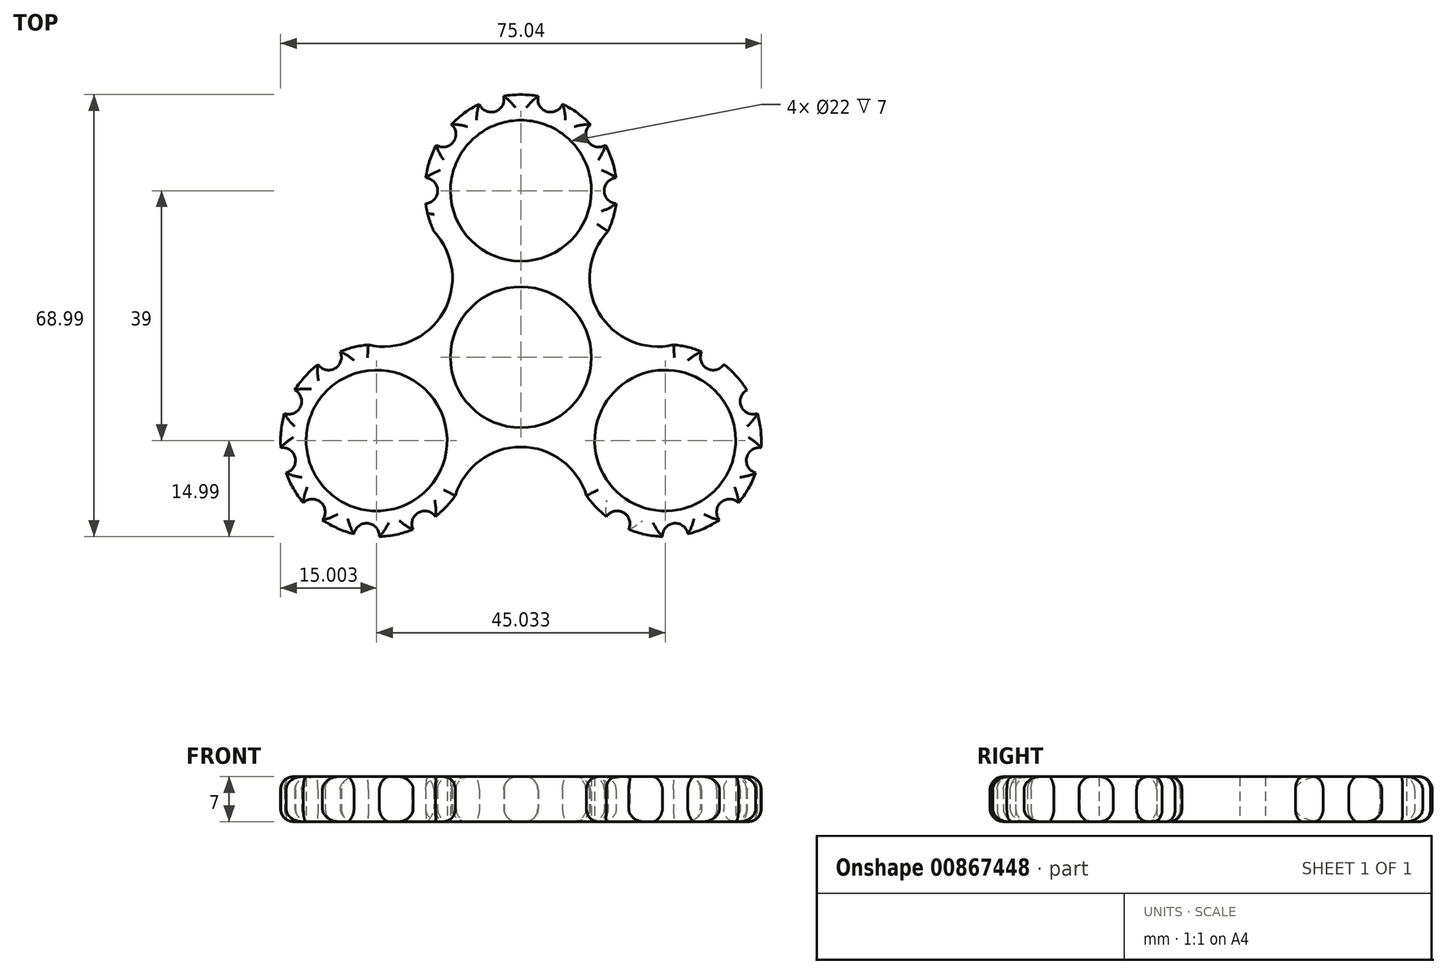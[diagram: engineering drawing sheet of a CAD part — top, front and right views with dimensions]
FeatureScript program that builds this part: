
annotation { "Feature Type Name" : "Feature", "Feature Type Description" : "" }
export const myFeature = defineFeature(function(context is Context, id is Id, definition is map)
    precondition{}
    {
        {
            var Q0;
            Q0=qCreatedBy(makeId("Top.planeOp"),FACE);
            var sketch = newSketch(context, id + "F0", { "sketchPlane" : qUnion([Q0])});
            skCircle(sketch, "E0", {"center": v(0, 0) * mm, "radius": 11 * mm});
            skCircle(sketch, "E1.0", {"center": v(0, 0) * mm, "radius": 14 * mm});
            skLineSegment(sketch, "E2", {"start": v(0, 0) * mm, "end": v(0, 26) * mm});
            skCircle(sketch, "E3", {"center": v(0, 26) * mm, "radius": 11 * mm});
            skCircle(sketch, "E4.0", {"center": v(0, 26) * mm, "radius": 15 * mm});
            skCircle(sketch, "E5", {"center": v(-15, 26) * mm, "radius": 2 * mm});
            skCircle(sketch, "E6.1.0", {"center": v(-12.14, 34.82) * mm, "radius": 2 * mm});
            skCircle(sketch, "E6.2.0", {"center": v(-4.64, 40.27) * mm, "radius": 2 * mm});
            skLineSegment(sketch, "E6.anchor1", {"start": v(0, 26) * mm, "end": v(-15, 26) * mm, "construction": true});
            skLineSegment(sketch, "E6.anchor2", {"start": v(0, 26) * mm, "end": v(15, 26) * mm, "construction": true});
            skCircle(sketch, "E7.1.3.0", {"center": v(4.64, 40.27) * mm, "radius": 2 * mm});
            skCircle(sketch, "E7.1.4.0", {"center": v(12.14, 34.82) * mm, "radius": 2 * mm});
            skPoint(sketch, "E8.center", {"position": v(-0.5, -0.29) * mm});
            skPoint(sketch, "E9", {"position": v(-14.87, 24) * mm});
            skLineSegment(sketch, "E10", {"start": v(0, 0) * mm, "end": v(12.12, 7) * mm});
            skPoint(sketch, "E11.MirrorP", {"position": v(14.87, 24) * mm});
            skCircle(sketch, "E12.1.5.0", {"center": v(15, 26) * mm, "radius": 2 * mm});
            skLineSegment(sketch, "E13", {"start": v(0, 26) * mm, "end": v(13.6, 19.66) * mm});
            skCircle(sketch, "E14.1.0", {"center": v(-22.52, -13) * mm, "radius": 15 * mm});
            skCircle(sketch, "E14.1.1", {"center": v(-22.52, -13) * mm, "radius": 11 * mm});
            skCircle(sketch, "E14.1.2", {"center": v(-15.02, -26) * mm, "radius": 2 * mm});
            skCircle(sketch, "E14.1.3", {"center": v(-24.08, -27.92) * mm, "radius": 2 * mm});
            skCircle(sketch, "E14.1.4", {"center": v(-32.55, -24.15) * mm, "radius": 2 * mm});
            skCircle(sketch, "E14.1.5", {"center": v(-37.19, -16.12) * mm, "radius": 2 * mm});
            skCircle(sketch, "E14.1.6", {"center": v(-36.22, -6.9) * mm, "radius": 2 * mm});
            skCircle(sketch, "E14.1.7", {"center": v(-30.02, 0) * mm, "radius": 2 * mm});
            skCircle(sketch, "E14.2.0", {"center": v(22.52, -13) * mm, "radius": 15 * mm});
            skCircle(sketch, "E14.2.1", {"center": v(22.52, -13) * mm, "radius": 11 * mm});
            skCircle(sketch, "E14.2.2", {"center": v(30.02, 0) * mm, "radius": 2 * mm});
            skCircle(sketch, "E14.2.3", {"center": v(36.22, -6.9) * mm, "radius": 2 * mm});
            skCircle(sketch, "E14.2.4", {"center": v(37.19, -16.12) * mm, "radius": 2 * mm});
            skCircle(sketch, "E14.2.5", {"center": v(32.55, -24.15) * mm, "radius": 2 * mm});
            skCircle(sketch, "E14.2.6", {"center": v(24.08, -27.92) * mm, "radius": 2 * mm});
            skCircle(sketch, "E14.2.7", {"center": v(15.02, -26) * mm, "radius": 2 * mm});
            skLineSegment(sketch, "E15.MirrorCS", {"start": v(22.52, -13) * mm, "end": v(23.82, 1.94) * mm});
            skArc(sketch, "E16", {"start": v(13.6, 19.66) * mm, "mid": v(12.12, 7) * mm, "end": v(23.82, 1.94) * mm});
            skArc(sketch, "E17.1.0", {"start": v(-23.82, 1.94) * mm, "mid": v(-12.12, 7) * mm, "end": v(-13.6, 19.66) * mm});
            skArc(sketch, "E17.2.0", {"start": v(10.23, -21.6) * mm, "mid": v(0, -14) * mm, "end": v(-10.23, -21.6) * mm});
            skSolve(sketch);
        }
        {
            var Q0;
            {var subQ3=sQuery(id+"F0.wireOp",EDGE,"E1.0");var subQ18=sQuery(id+"F0.wireOp",EDGE,"E2");var subQ19=makeQuery(id+"F0.imprint","INTERSECT",VERTEX,{"derivedFrom":[subQ3,subQ18]});Q0=makeQuery(id+"F0.imprint","IMPRINT",FACE,{"disambiguationData":[TD([[makeQuery(id+"F0.imprint","IMPRINT",EDGE,{"disambiguationData":[TD([[subQ19,-1.0]])],"derivedFrom":subQ3}),-1.0]])]});}
            var Q1;
            {var subQ5=sQuery(id+"F0.wireOp",EDGE,"E1.0");var subQ7=sQuery(id+"F0.wireOp",EDGE,"E4.0");var subQ8=makeQuery(id+"F0.imprint","INTERSECT",VERTEX,{"disambiguationData":[OD(0.0)],"derivedFrom":[subQ5,subQ7]});Q1=makeQuery(id+"F0.imprint","IMPRINT",FACE,{"disambiguationData":[TD([[makeQuery(id+"F0.imprint","IMPRINT",EDGE,{"disambiguationData":[TD([[subQ8,-1.0]])],"derivedFrom":subQ5}),-1.0]])]});}
            var Q2;
            {var subQ0=sQuery(id+"F0.wireOp",EDGE,"E4.0");var subQ1=sQuery(id+"F0.wireOp",EDGE,"E1.0");var subQ2=makeQuery(id+"F0.imprint","INTERSECT",VERTEX,{"disambiguationData":[OD(0.0)],"derivedFrom":[subQ1,subQ0]});Q2=makeQuery(id+"F0.imprint","IMPRINT",FACE,{"disambiguationData":[TD([[makeQuery(id+"F0.imprint","IMPRINT",EDGE,{"disambiguationData":[TD([[subQ2,-1.0]])],"derivedFrom":subQ1}),1.0]])]});}
            var Q3;
            {var subQ0=sQuery(id+"F0.wireOp",EDGE,"E2");var subQ1=sQuery(id+"F0.wireOp",EDGE,"E1.0");var subQ2=makeQuery(id+"F0.imprint","INTERSECT",VERTEX,{"derivedFrom":[subQ1,subQ0]});Q3=makeQuery(id+"F0.imprint","IMPRINT",FACE,{"disambiguationData":[TD([[makeQuery(id+"F0.imprint","IMPRINT",EDGE,{"disambiguationData":[TD([[subQ2,-1.0]])],"derivedFrom":subQ1}),1.0]])]});}
            var Q4;
            {var subQ0=sQuery(id+"F0.wireOp",EDGE,"E17.1.0");var subQ1=sQuery(id+"F0.wireOp",EDGE,"E1.0");var subQ2=makeQuery(id+"F0.imprint","INTERSECT",VERTEX,{"derivedFrom":[subQ1,subQ0]});Q4=makeQuery(id+"F0.imprint","IMPRINT",FACE,{"disambiguationData":[TD([[makeQuery(id+"F0.imprint","IMPRINT",EDGE,{"disambiguationData":[TD([[subQ2,1.0]])],"derivedFrom":subQ1}),-1.0]])]});}
            var Q5;
            {var subQ1=sQuery(id+"F0.wireOp",EDGE,"E1.0");var subQ5=makeQuery(id+"F0.imprint","INTERSECT",VERTEX,{"derivedFrom":[subQ1,sQuery(id+"F0.wireOp",EDGE,"E17.1.0")]});Q5=makeQuery(id+"F0.imprint","IMPRINT",FACE,{"disambiguationData":[TD([[makeQuery(id+"F0.imprint","IMPRINT",EDGE,{"disambiguationData":[TD([[subQ5,1.0]])],"derivedFrom":subQ1}),1.0]])]});}
            var Q6;
            {var subQ0=sQuery(id+"F0.wireOp",EDGE,"E17.1.0");var subQ1=sQuery(id+"F0.wireOp",EDGE,"E1.0");var subQ2=makeQuery(id+"F0.imprint","INTERSECT",VERTEX,{"derivedFrom":[subQ1,subQ0]});Q6=makeQuery(id+"F0.imprint","IMPRINT",FACE,{"disambiguationData":[TD([[makeQuery(id+"F0.imprint","IMPRINT",EDGE,{"disambiguationData":[TD([[subQ2,-1.0]])],"derivedFrom":subQ1}),-1.0]])]});}
            var Q7;
            Q7=makeQuery(id+"F0.imprint","IMPRINT",FACE,{"disambiguationData":[TD([[makeQuery(id+"F0.imprint","IMPRINT",EDGE,{"derivedFrom":sQuery(id+"F0.wireOp",EDGE,"E14.1.1")}),-1.0]])]});
            var Q8;
            {var subQ0=sQuery(id+"F0.wireOp",EDGE,"E14.1.0");var subQ1=sQuery(id+"F0.wireOp",EDGE,"E1.0");var subQ2=makeQuery(id+"F0.imprint","INTERSECT",VERTEX,{"disambiguationData":[OD(0.0)],"derivedFrom":[subQ1,subQ0]});Q8=makeQuery(id+"F0.imprint","IMPRINT",FACE,{"disambiguationData":[TD([[makeQuery(id+"F0.imprint","IMPRINT",EDGE,{"disambiguationData":[TD([[subQ2,-1.0]])],"derivedFrom":subQ1}),1.0]])]});}
            var Q9;
            {var subQ0=sQuery(id+"F0.wireOp",EDGE,"E14.1.0");var subQ1=sQuery(id+"F0.wireOp",EDGE,"E0");var subQ2=makeQuery(id+"F0.imprint","INTERSECT",VERTEX,{"derivedFrom":[subQ1,subQ0]});Q9=makeQuery(id+"F0.imprint","IMPRINT",FACE,{"disambiguationData":[TD([[makeQuery(id+"F0.imprint","IMPRINT",EDGE,{"disambiguationData":[TD([[subQ2,-1.0]])],"derivedFrom":subQ1}),-1.0]])]});}
            var Q10;
            {var subQ0=sQuery(id+"F0.wireOp",EDGE,"E17.2.0");var subQ1=sQuery(id+"F0.wireOp",EDGE,"E1.0");var subQ2=makeQuery(id+"F0.imprint","INTERSECT",VERTEX,{"derivedFrom":[subQ1,subQ0]});Q10=makeQuery(id+"F0.imprint","IMPRINT",FACE,{"disambiguationData":[TD([[makeQuery(id+"F0.imprint","IMPRINT",EDGE,{"disambiguationData":[TD([[subQ2,1.0]])],"derivedFrom":subQ1}),-1.0]])]});}
            var Q11;
            {var subQ0=sQuery(id+"F0.wireOp",EDGE,"E17.2.0");var subQ1=sQuery(id+"F0.wireOp",EDGE,"E1.0");var subQ2=makeQuery(id+"F0.imprint","INTERSECT",VERTEX,{"derivedFrom":[subQ1,subQ0]});Q11=makeQuery(id+"F0.imprint","IMPRINT",FACE,{"disambiguationData":[TD([[makeQuery(id+"F0.imprint","IMPRINT",EDGE,{"disambiguationData":[TD([[subQ2,-1.0]])],"derivedFrom":subQ1}),-1.0]])]});}
            var Q12;
            Q12=makeQuery(id+"F0.imprint","IMPRINT",FACE,{"disambiguationData":[TD([[makeQuery(id+"F0.imprint","IMPRINT",EDGE,{"derivedFrom":sQuery(id+"F0.wireOp",EDGE,"E14.2.1")}),-1.0]])]});
            var Q13;
            {var subQ0=sQuery(id+"F0.wireOp",EDGE,"E14.2.0");var subQ1=sQuery(id+"F0.wireOp",EDGE,"E1.0");var subQ2=makeQuery(id+"F0.imprint","INTERSECT",VERTEX,{"disambiguationData":[OD(0.0)],"derivedFrom":[subQ1,subQ0]});Q13=makeQuery(id+"F0.imprint","IMPRINT",FACE,{"disambiguationData":[TD([[makeQuery(id+"F0.imprint","IMPRINT",EDGE,{"disambiguationData":[TD([[subQ2,-1.0]])],"derivedFrom":subQ1}),1.0]])]});}
            var Q14;
            {var subQ0=sQuery(id+"F0.wireOp",EDGE,"E16");var subQ3=sQuery(id+"F0.wireOp",EDGE,"E14.2.0");var subQ5=makeQuery(id+"F0.imprint","INTERSECT",VERTEX,{"disambiguationData":[OD(1.0)],"derivedFrom":[subQ3,subQ0]});Q14=makeQuery(id+"F0.imprint","IMPRINT",FACE,{"disambiguationData":[TD([[makeQuery(id+"F0.imprint","IMPRINT",EDGE,{"disambiguationData":[TD([[subQ5,-1.0]])],"derivedFrom":subQ3}),-1.0]])]});}
            var Q15;
            {var subQ0=sQuery(id+"F0.wireOp",EDGE,"E10");var subQ1=sQuery(id+"F0.wireOp",EDGE,"E0");var subQ2=makeQuery(id+"F0.imprint","INTERSECT",VERTEX,{"derivedFrom":[subQ1,subQ0]});Q15=makeQuery(id+"F0.imprint","IMPRINT",FACE,{"disambiguationData":[TD([[makeQuery(id+"F0.imprint","IMPRINT",EDGE,{"disambiguationData":[TD([[subQ2,1.0]])],"derivedFrom":subQ1}),-1.0]])]});}
            var Q16;
            {var subQ0=sQuery(id+"F0.wireOp",EDGE,"E16");var subQ3=sQuery(id+"F0.wireOp",EDGE,"E4.0");var subQ5=makeQuery(id+"F0.imprint","INTERSECT",VERTEX,{"derivedFrom":[subQ3,subQ0]});Q16=makeQuery(id+"F0.imprint","IMPRINT",FACE,{"disambiguationData":[TD([[makeQuery(id+"F0.imprint","IMPRINT",EDGE,{"disambiguationData":[TD([[subQ5,1.0]])],"derivedFrom":subQ3}),-1.0]])]});}
            var Q17;
            {var subQ0=sQuery(id+"F0.wireOp",EDGE,"E10");var subQ1=sQuery(id+"F0.wireOp",EDGE,"E0");var subQ2=makeQuery(id+"F0.imprint","INTERSECT",VERTEX,{"derivedFrom":[subQ1,subQ0]});Q17=makeQuery(id+"F0.imprint","IMPRINT",FACE,{"disambiguationData":[TD([[makeQuery(id+"F0.imprint","IMPRINT",EDGE,{"disambiguationData":[TD([[subQ2,-1.0]])],"derivedFrom":subQ1}),-1.0]])]});}
            extrude(context, id + "F1", {"entities" : qUnion([Q0, Q1, Q2, Q3, Q4, Q5, Q6, Q7, Q8, Q9, Q10, Q11, Q12, Q13, Q14, Q15, Q16, Q17]), "depth" : 7 * mm, "offsetDistance" : 25 * mm});
        }
        {
            var Q0;
            Q0=makeQuery(id+"F1.opExtrude","CAP_EDGE",EDGE,{"disambiguationData":[OSD([sQuery(id+"F0.wireOp",EDGE,"E17.1.0")])],"isStart":false});
            var Q1;
            {var subQ0=sQuery(id+"F0.wireOp",EDGE,"E4.0");Q1=makeQuery(id+"F1.opExtrude","CAP_EDGE",EDGE,{"disambiguationData":[OSD([subQ0]),TDD([makeQuery(id+"F0.imprint","IMPRINT",EDGE,{"disambiguationData":[TD([[makeQuery(id+"F0.imprint","INTERSECT",VERTEX,{"disambiguationData":[OD(0.0)],"derivedFrom":[subQ0,sQuery(id+"F0.wireOp",EDGE,"E17.1.0")]}),1.0]])],"derivedFrom":subQ0})])],"isStart":false});}
            var Q2;
            Q2=makeQuery(id+"F1.opExtrude","CAP_EDGE",EDGE,{"disambiguationData":[OSD([sQuery(id+"F0.wireOp",EDGE,"E5")])],"isStart":false});
            var Q3;
            {var subQ0=sQuery(id+"F0.wireOp",EDGE,"E4.0");Q3=makeQuery(id+"F1.opExtrude","CAP_EDGE",EDGE,{"disambiguationData":[OSD([subQ0]),TDD([makeQuery(id+"F0.imprint","IMPRINT",EDGE,{"disambiguationData":[TD([[makeQuery(id+"F0.imprint","INTERSECT",VERTEX,{"disambiguationData":[OD(1.0)],"derivedFrom":[subQ0,sQuery(id+"F0.wireOp",EDGE,"E6.1.0")]}),-1.0]])],"derivedFrom":subQ0})])],"isStart":false});}
            var Q4;
            Q4=makeQuery(id+"F1.opExtrude","CAP_EDGE",EDGE,{"disambiguationData":[OSD([sQuery(id+"F0.wireOp",EDGE,"E6.1.0")])],"isStart":false});
            var Q5;
            {var subQ0=sQuery(id+"F0.wireOp",EDGE,"E4.0");Q5=makeQuery(id+"F1.opExtrude","CAP_EDGE",EDGE,{"disambiguationData":[OSD([subQ0]),TDD([makeQuery(id+"F0.imprint","IMPRINT",EDGE,{"disambiguationData":[TD([[makeQuery(id+"F0.imprint","INTERSECT",VERTEX,{"disambiguationData":[OD(1.0)],"derivedFrom":[subQ0,sQuery(id+"F0.wireOp",EDGE,"E6.2.0")]}),-1.0]])],"derivedFrom":subQ0})])],"isStart":false});}
            var Q6;
            Q6=makeQuery(id+"F1.opExtrude","CAP_EDGE",EDGE,{"disambiguationData":[OSD([sQuery(id+"F0.wireOp",EDGE,"E6.2.0")])],"isStart":false});
            var Q7;
            {var subQ0=sQuery(id+"F0.wireOp",EDGE,"E4.0");Q7=makeQuery(id+"F1.opExtrude","CAP_EDGE",EDGE,{"disambiguationData":[OSD([subQ0]),TDD([makeQuery(id+"F0.imprint","IMPRINT",EDGE,{"disambiguationData":[TD([[makeQuery(id+"F0.imprint","INTERSECT",VERTEX,{"disambiguationData":[OD(1.0)],"derivedFrom":[subQ0,sQuery(id+"F0.wireOp",EDGE,"E7.1.3.0")]}),-1.0]])],"derivedFrom":subQ0})])],"isStart":false});}
            var Q8;
            Q8=makeQuery(id+"F1.opExtrude","CAP_EDGE",EDGE,{"disambiguationData":[OSD([sQuery(id+"F0.wireOp",EDGE,"E7.1.3.0")])],"isStart":false});
            var Q9;
            {var subQ0=sQuery(id+"F0.wireOp",EDGE,"E4.0");Q9=makeQuery(id+"F1.opExtrude","CAP_EDGE",EDGE,{"disambiguationData":[OSD([subQ0]),TDD([makeQuery(id+"F0.imprint","IMPRINT",EDGE,{"disambiguationData":[TD([[makeQuery(id+"F0.imprint","INTERSECT",VERTEX,{"disambiguationData":[OD(1.0)],"derivedFrom":[subQ0,sQuery(id+"F0.wireOp",EDGE,"E7.1.4.0")]}),-1.0]])],"derivedFrom":subQ0})])],"isStart":false});}
            var Q10;
            Q10=makeQuery(id+"F1.opExtrude","CAP_EDGE",EDGE,{"disambiguationData":[OSD([sQuery(id+"F0.wireOp",EDGE,"E7.1.4.0")])],"isStart":false});
            var Q11;
            {var subQ0=sQuery(id+"F0.wireOp",EDGE,"E4.0");Q11=makeQuery(id+"F1.opExtrude","CAP_EDGE",EDGE,{"disambiguationData":[OSD([subQ0]),TDD([makeQuery(id+"F0.imprint","IMPRINT",EDGE,{"disambiguationData":[TD([[makeQuery(id+"F0.imprint","INTERSECT",VERTEX,{"disambiguationData":[OD(0.0)],"derivedFrom":[subQ0,sQuery(id+"F0.wireOp",EDGE,"E7.1.4.0")]}),1.0]])],"derivedFrom":subQ0})])],"isStart":false});}
            var Q12;
            Q12=makeQuery(id+"F1.opExtrude","CAP_EDGE",EDGE,{"disambiguationData":[OSD([sQuery(id+"F0.wireOp",EDGE,"E12.1.5.0")])],"isStart":false});
            var Q13;
            {var subQ0=sQuery(id+"F0.wireOp",EDGE,"E4.0");Q13=makeQuery(id+"F1.opExtrude","CAP_EDGE",EDGE,{"disambiguationData":[OSD([subQ0]),TDD([makeQuery(id+"F0.imprint","IMPRINT",EDGE,{"disambiguationData":[TD([[makeQuery(id+"F0.imprint","INTERSECT",VERTEX,{"disambiguationData":[OD(1.0)],"derivedFrom":[subQ0,sQuery(id+"F0.wireOp",EDGE,"E12.1.5.0")]}),1.0]])],"derivedFrom":subQ0})])],"isStart":false});}
            var Q14;
            Q14=makeQuery(id+"F1.opExtrude","CAP_EDGE",EDGE,{"disambiguationData":[OSD([sQuery(id+"F0.wireOp",EDGE,"E16")])],"isStart":false});
            var Q15;
            {var subQ0=sQuery(id+"F0.wireOp",EDGE,"E14.2.0");Q15=makeQuery(id+"F1.opExtrude","CAP_EDGE",EDGE,{"disambiguationData":[OSD([subQ0]),TDD([makeQuery(id+"F0.imprint","IMPRINT",EDGE,{"disambiguationData":[TD([[makeQuery(id+"F0.imprint","INTERSECT",VERTEX,{"disambiguationData":[OD(0.0)],"derivedFrom":[subQ0,sQuery(id+"F0.wireOp",EDGE,"E16")]}),1.0]])],"derivedFrom":subQ0})])],"isStart":false});}
            var Q16;
            Q16=makeQuery(id+"F1.opExtrude","CAP_EDGE",EDGE,{"disambiguationData":[OSD([sQuery(id+"F0.wireOp",EDGE,"E14.2.2")])],"isStart":false});
            var Q17;
            {var subQ0=sQuery(id+"F0.wireOp",EDGE,"E14.2.0");Q17=makeQuery(id+"F1.opExtrude","CAP_EDGE",EDGE,{"disambiguationData":[OSD([subQ0]),TDD([makeQuery(id+"F0.imprint","IMPRINT",EDGE,{"disambiguationData":[TD([[makeQuery(id+"F0.imprint","INTERSECT",VERTEX,{"disambiguationData":[OD(1.0)],"derivedFrom":[subQ0,sQuery(id+"F0.wireOp",EDGE,"E14.2.3")]}),-1.0]])],"derivedFrom":subQ0})])],"isStart":false});}
            var Q18;
            Q18=makeQuery(id+"F1.opExtrude","CAP_EDGE",EDGE,{"disambiguationData":[OSD([sQuery(id+"F0.wireOp",EDGE,"E14.2.3")])],"isStart":false});
            var Q19;
            {var subQ0=sQuery(id+"F0.wireOp",EDGE,"E14.2.0");Q19=makeQuery(id+"F1.opExtrude","CAP_EDGE",EDGE,{"disambiguationData":[OSD([subQ0]),TDD([makeQuery(id+"F0.imprint","IMPRINT",EDGE,{"disambiguationData":[TD([[makeQuery(id+"F0.imprint","INTERSECT",VERTEX,{"disambiguationData":[OD(1.0)],"derivedFrom":[subQ0,sQuery(id+"F0.wireOp",EDGE,"E14.2.4")]}),-1.0]])],"derivedFrom":subQ0})])],"isStart":false});}
            var Q20;
            Q20=makeQuery(id+"F1.opExtrude","CAP_EDGE",EDGE,{"disambiguationData":[OSD([sQuery(id+"F0.wireOp",EDGE,"E14.2.4")])],"isStart":false});
            var Q21;
            {var subQ0=sQuery(id+"F0.wireOp",EDGE,"E14.2.0");Q21=makeQuery(id+"F1.opExtrude","CAP_EDGE",EDGE,{"disambiguationData":[OSD([subQ0]),TDD([makeQuery(id+"F0.imprint","IMPRINT",EDGE,{"disambiguationData":[TD([[makeQuery(id+"F0.imprint","INTERSECT",VERTEX,{"disambiguationData":[OD(1.0)],"derivedFrom":[subQ0,sQuery(id+"F0.wireOp",EDGE,"E14.2.5")]}),-1.0]])],"derivedFrom":subQ0})])],"isStart":false});}
            var Q22;
            Q22=makeQuery(id+"F1.opExtrude","CAP_EDGE",EDGE,{"disambiguationData":[OSD([sQuery(id+"F0.wireOp",EDGE,"E14.2.5")])],"isStart":false});
            var Q23;
            {var subQ0=sQuery(id+"F0.wireOp",EDGE,"E14.2.0");Q23=makeQuery(id+"F1.opExtrude","CAP_EDGE",EDGE,{"disambiguationData":[OSD([subQ0]),TDD([makeQuery(id+"F0.imprint","IMPRINT",EDGE,{"disambiguationData":[TD([[makeQuery(id+"F0.imprint","INTERSECT",VERTEX,{"disambiguationData":[OD(1.0)],"derivedFrom":[subQ0,sQuery(id+"F0.wireOp",EDGE,"E14.2.6")]}),-1.0]])],"derivedFrom":subQ0})])],"isStart":false});}
            var Q24;
            Q24=makeQuery(id+"F1.opExtrude","CAP_EDGE",EDGE,{"disambiguationData":[OSD([sQuery(id+"F0.wireOp",EDGE,"E14.2.6")])],"isStart":false});
            var Q25;
            {var subQ0=sQuery(id+"F0.wireOp",EDGE,"E14.2.0");Q25=makeQuery(id+"F1.opExtrude","CAP_EDGE",EDGE,{"disambiguationData":[OSD([subQ0]),TDD([makeQuery(id+"F0.imprint","IMPRINT",EDGE,{"disambiguationData":[TD([[makeQuery(id+"F0.imprint","INTERSECT",VERTEX,{"disambiguationData":[OD(0.0)],"derivedFrom":[subQ0,sQuery(id+"F0.wireOp",EDGE,"E14.2.6")]}),1.0]])],"derivedFrom":subQ0})])],"isStart":false});}
            var Q26;
            {var subQ0=sQuery(id+"F0.wireOp",EDGE,"E14.2.0");Q26=makeQuery(id+"F1.opExtrude","CAP_EDGE",EDGE,{"disambiguationData":[OSD([subQ0]),TDD([makeQuery(id+"F0.imprint","IMPRINT",EDGE,{"disambiguationData":[TD([[makeQuery(id+"F0.imprint","INTERSECT",VERTEX,{"disambiguationData":[OD(0.0)],"derivedFrom":[subQ0,sQuery(id+"F0.wireOp",EDGE,"E17.2.0")]}),-1.0]])],"derivedFrom":subQ0})])],"isStart":false});}
            var Q27;
            Q27=makeQuery(id+"F1.opExtrude","CAP_EDGE",EDGE,{"disambiguationData":[OSD([sQuery(id+"F0.wireOp",EDGE,"E17.2.0")])],"isStart":false});
            var Q28;
            {var subQ0=sQuery(id+"F0.wireOp",EDGE,"E14.1.0");Q28=makeQuery(id+"F1.opExtrude","CAP_EDGE",EDGE,{"disambiguationData":[OSD([subQ0]),TDD([makeQuery(id+"F0.imprint","IMPRINT",EDGE,{"disambiguationData":[TD([[makeQuery(id+"F0.imprint","INTERSECT",VERTEX,{"disambiguationData":[OD(0.0)],"derivedFrom":[subQ0,sQuery(id+"F0.wireOp",EDGE,"E17.2.0")]}),1.0]])],"derivedFrom":subQ0})])],"isStart":false});}
            var Q29;
            Q29=makeQuery(id+"F1.opExtrude","CAP_EDGE",EDGE,{"disambiguationData":[OSD([sQuery(id+"F0.wireOp",EDGE,"E14.1.2")])],"isStart":false});
            var Q30;
            {var subQ0=sQuery(id+"F0.wireOp",EDGE,"E14.1.0");Q30=makeQuery(id+"F1.opExtrude","CAP_EDGE",EDGE,{"disambiguationData":[OSD([subQ0]),TDD([makeQuery(id+"F0.imprint","IMPRINT",EDGE,{"disambiguationData":[TD([[makeQuery(id+"F0.imprint","INTERSECT",VERTEX,{"disambiguationData":[OD(1.0)],"derivedFrom":[subQ0,sQuery(id+"F0.wireOp",EDGE,"E14.1.3")]}),-1.0]])],"derivedFrom":subQ0})])],"isStart":false});}
            var Q31;
            Q31=makeQuery(id+"F1.opExtrude","CAP_EDGE",EDGE,{"disambiguationData":[OSD([sQuery(id+"F0.wireOp",EDGE,"E14.1.3")])],"isStart":false});
            var Q32;
            {var subQ0=sQuery(id+"F0.wireOp",EDGE,"E14.1.0");Q32=makeQuery(id+"F1.opExtrude","CAP_EDGE",EDGE,{"disambiguationData":[OSD([subQ0]),TDD([makeQuery(id+"F0.imprint","IMPRINT",EDGE,{"disambiguationData":[TD([[makeQuery(id+"F0.imprint","INTERSECT",VERTEX,{"disambiguationData":[OD(1.0)],"derivedFrom":[subQ0,sQuery(id+"F0.wireOp",EDGE,"E14.1.4")]}),-1.0]])],"derivedFrom":subQ0})])],"isStart":false});}
            var Q33;
            Q33=makeQuery(id+"F1.opExtrude","CAP_EDGE",EDGE,{"disambiguationData":[OSD([sQuery(id+"F0.wireOp",EDGE,"E14.1.4")])],"isStart":false});
            var Q34;
            {var subQ0=sQuery(id+"F0.wireOp",EDGE,"E14.1.0");Q34=makeQuery(id+"F1.opExtrude","CAP_EDGE",EDGE,{"disambiguationData":[OSD([subQ0]),TDD([makeQuery(id+"F0.imprint","IMPRINT",EDGE,{"disambiguationData":[TD([[makeQuery(id+"F0.imprint","INTERSECT",VERTEX,{"disambiguationData":[OD(1.0)],"derivedFrom":[subQ0,sQuery(id+"F0.wireOp",EDGE,"E14.1.5")]}),-1.0]])],"derivedFrom":subQ0})])],"isStart":false});}
            var Q35;
            Q35=makeQuery(id+"F1.opExtrude","CAP_EDGE",EDGE,{"disambiguationData":[OSD([sQuery(id+"F0.wireOp",EDGE,"E14.1.5")])],"isStart":false});
            var Q36;
            {var subQ0=sQuery(id+"F0.wireOp",EDGE,"E14.1.0");Q36=makeQuery(id+"F1.opExtrude","CAP_EDGE",EDGE,{"disambiguationData":[OSD([subQ0]),TDD([makeQuery(id+"F0.imprint","IMPRINT",EDGE,{"disambiguationData":[TD([[makeQuery(id+"F0.imprint","INTERSECT",VERTEX,{"disambiguationData":[OD(1.0)],"derivedFrom":[subQ0,sQuery(id+"F0.wireOp",EDGE,"E14.1.6")]}),-1.0]])],"derivedFrom":subQ0})])],"isStart":false});}
            var Q37;
            Q37=makeQuery(id+"F1.opExtrude","CAP_EDGE",EDGE,{"disambiguationData":[OSD([sQuery(id+"F0.wireOp",EDGE,"E14.1.6")])],"isStart":false});
            var Q38;
            {var subQ0=sQuery(id+"F0.wireOp",EDGE,"E14.1.0");Q38=makeQuery(id+"F1.opExtrude","CAP_EDGE",EDGE,{"disambiguationData":[OSD([subQ0]),TDD([makeQuery(id+"F0.imprint","IMPRINT",EDGE,{"disambiguationData":[TD([[makeQuery(id+"F0.imprint","INTERSECT",VERTEX,{"disambiguationData":[OD(0.0)],"derivedFrom":[subQ0,sQuery(id+"F0.wireOp",EDGE,"E14.1.6")]}),1.0]])],"derivedFrom":subQ0})])],"isStart":false});}
            var Q39;
            Q39=makeQuery(id+"F1.opExtrude","CAP_EDGE",EDGE,{"disambiguationData":[OSD([sQuery(id+"F0.wireOp",EDGE,"E14.1.7")])],"isStart":false});
            var Q40;
            {var subQ0=sQuery(id+"F0.wireOp",EDGE,"E14.1.0");Q40=makeQuery(id+"F1.opExtrude","CAP_EDGE",EDGE,{"disambiguationData":[OSD([subQ0]),TDD([makeQuery(id+"F0.imprint","IMPRINT",EDGE,{"disambiguationData":[TD([[makeQuery(id+"F0.imprint","INTERSECT",VERTEX,{"disambiguationData":[OD(0.0)],"derivedFrom":[subQ0,sQuery(id+"F0.wireOp",EDGE,"E17.1.0")]}),-1.0]])],"derivedFrom":subQ0})])],"isStart":false});}
            fillet(context, id + "F2", {"entities" : qUnion([Q0, Q1, Q2, Q3, Q4, Q5, Q6, Q7, Q8, Q9, Q10, Q11, Q12, Q13, Q14, Q15, Q16, Q17, Q18, Q19, Q20, Q21, Q22, Q23, Q24, Q25, Q26, Q27, Q28, Q29, Q30, Q31, Q32, Q33, Q34, Q35, Q36, Q37, Q38, Q39, Q40]), "radius" : 2 * mm, "tangentPropagation" : true, "allowEdgeOverflow" : false});
        }
        {
            var Q0;
            {var subQ0=sQuery(id+"F0.wireOp",EDGE,"E4.0");Q0=makeQuery(id+"F1.opExtrude","CAP_EDGE",EDGE,{"disambiguationData":[OSD([subQ0]),TDD([makeQuery(id+"F0.imprint","IMPRINT",EDGE,{"disambiguationData":[TD([[makeQuery(id+"F0.imprint","INTERSECT",VERTEX,{"disambiguationData":[OD(1.0)],"derivedFrom":[subQ0,sQuery(id+"F0.wireOp",EDGE,"E6.2.0")]}),-1.0]])],"derivedFrom":subQ0})])],"isStart":true});}
            var Q1;
            Q1=makeQuery(id+"F1.opExtrude","CAP_EDGE",EDGE,{"disambiguationData":[OSD([sQuery(id+"F0.wireOp",EDGE,"E6.2.0")])],"isStart":true});
            var Q2;
            {var subQ0=sQuery(id+"F0.wireOp",EDGE,"E4.0");Q2=makeQuery(id+"F1.opExtrude","CAP_EDGE",EDGE,{"disambiguationData":[OSD([subQ0]),TDD([makeQuery(id+"F0.imprint","IMPRINT",EDGE,{"disambiguationData":[TD([[makeQuery(id+"F0.imprint","INTERSECT",VERTEX,{"disambiguationData":[OD(1.0)],"derivedFrom":[subQ0,sQuery(id+"F0.wireOp",EDGE,"E7.1.3.0")]}),-1.0]])],"derivedFrom":subQ0})])],"isStart":true});}
            var Q3;
            Q3=makeQuery(id+"F1.opExtrude","CAP_EDGE",EDGE,{"disambiguationData":[OSD([sQuery(id+"F0.wireOp",EDGE,"E7.1.3.0")])],"isStart":true});
            var Q4;
            {var subQ0=sQuery(id+"F0.wireOp",EDGE,"E4.0");Q4=makeQuery(id+"F1.opExtrude","CAP_EDGE",EDGE,{"disambiguationData":[OSD([subQ0]),TDD([makeQuery(id+"F0.imprint","IMPRINT",EDGE,{"disambiguationData":[TD([[makeQuery(id+"F0.imprint","INTERSECT",VERTEX,{"disambiguationData":[OD(1.0)],"derivedFrom":[subQ0,sQuery(id+"F0.wireOp",EDGE,"E7.1.4.0")]}),-1.0]])],"derivedFrom":subQ0})])],"isStart":true});}
            var Q5;
            Q5=makeQuery(id+"F1.opExtrude","CAP_EDGE",EDGE,{"disambiguationData":[OSD([sQuery(id+"F0.wireOp",EDGE,"E7.1.4.0")])],"isStart":true});
            var Q6;
            {var subQ0=sQuery(id+"F0.wireOp",EDGE,"E4.0");Q6=makeQuery(id+"F1.opExtrude","CAP_EDGE",EDGE,{"disambiguationData":[OSD([subQ0]),TDD([makeQuery(id+"F0.imprint","IMPRINT",EDGE,{"disambiguationData":[TD([[makeQuery(id+"F0.imprint","INTERSECT",VERTEX,{"disambiguationData":[OD(0.0)],"derivedFrom":[subQ0,sQuery(id+"F0.wireOp",EDGE,"E7.1.4.0")]}),1.0]])],"derivedFrom":subQ0})])],"isStart":true});}
            var Q7;
            Q7=makeQuery(id+"F1.opExtrude","CAP_EDGE",EDGE,{"disambiguationData":[OSD([sQuery(id+"F0.wireOp",EDGE,"E12.1.5.0")])],"isStart":true});
            var Q8;
            {var subQ0=sQuery(id+"F0.wireOp",EDGE,"E4.0");Q8=makeQuery(id+"F1.opExtrude","CAP_EDGE",EDGE,{"disambiguationData":[OSD([subQ0]),TDD([makeQuery(id+"F0.imprint","IMPRINT",EDGE,{"disambiguationData":[TD([[makeQuery(id+"F0.imprint","INTERSECT",VERTEX,{"disambiguationData":[OD(1.0)],"derivedFrom":[subQ0,sQuery(id+"F0.wireOp",EDGE,"E12.1.5.0")]}),1.0]])],"derivedFrom":subQ0})])],"isStart":true});}
            var Q9;
            Q9=makeQuery(id+"F1.opExtrude","CAP_EDGE",EDGE,{"disambiguationData":[OSD([sQuery(id+"F0.wireOp",EDGE,"E16")])],"isStart":true});
            var Q10;
            Q10=makeQuery(id+"F1.opExtrude","CAP_EDGE",EDGE,{"disambiguationData":[OSD([sQuery(id+"F0.wireOp",EDGE,"E6.1.0")])],"isStart":true});
            var Q11;
            {var subQ0=sQuery(id+"F0.wireOp",EDGE,"E4.0");Q11=makeQuery(id+"F1.opExtrude","CAP_EDGE",EDGE,{"disambiguationData":[OSD([subQ0]),TDD([makeQuery(id+"F0.imprint","IMPRINT",EDGE,{"disambiguationData":[TD([[makeQuery(id+"F0.imprint","INTERSECT",VERTEX,{"disambiguationData":[OD(1.0)],"derivedFrom":[subQ0,sQuery(id+"F0.wireOp",EDGE,"E6.1.0")]}),-1.0]])],"derivedFrom":subQ0})])],"isStart":true});}
            var Q12;
            Q12=makeQuery(id+"F1.opExtrude","CAP_EDGE",EDGE,{"disambiguationData":[OSD([sQuery(id+"F0.wireOp",EDGE,"E5")])],"isStart":true});
            var Q13;
            {var subQ0=sQuery(id+"F0.wireOp",EDGE,"E4.0");Q13=makeQuery(id+"F1.opExtrude","CAP_EDGE",EDGE,{"disambiguationData":[OSD([subQ0]),TDD([makeQuery(id+"F0.imprint","IMPRINT",EDGE,{"disambiguationData":[TD([[makeQuery(id+"F0.imprint","INTERSECT",VERTEX,{"disambiguationData":[OD(0.0)],"derivedFrom":[subQ0,sQuery(id+"F0.wireOp",EDGE,"E17.1.0")]}),1.0]])],"derivedFrom":subQ0})])],"isStart":true});}
            var Q14;
            Q14=makeQuery(id+"F1.opExtrude","CAP_EDGE",EDGE,{"disambiguationData":[OSD([sQuery(id+"F0.wireOp",EDGE,"E17.1.0")])],"isStart":true});
            var Q15;
            {var subQ0=sQuery(id+"F0.wireOp",EDGE,"E14.1.0");Q15=makeQuery(id+"F1.opExtrude","CAP_EDGE",EDGE,{"disambiguationData":[OSD([subQ0]),TDD([makeQuery(id+"F0.imprint","IMPRINT",EDGE,{"disambiguationData":[TD([[makeQuery(id+"F0.imprint","INTERSECT",VERTEX,{"disambiguationData":[OD(0.0)],"derivedFrom":[subQ0,sQuery(id+"F0.wireOp",EDGE,"E17.1.0")]}),-1.0]])],"derivedFrom":subQ0})])],"isStart":true});}
            var Q16;
            Q16=makeQuery(id+"F1.opExtrude","CAP_EDGE",EDGE,{"disambiguationData":[OSD([sQuery(id+"F0.wireOp",EDGE,"E14.1.7")])],"isStart":true});
            var Q17;
            {var subQ0=sQuery(id+"F0.wireOp",EDGE,"E14.1.0");Q17=makeQuery(id+"F1.opExtrude","CAP_EDGE",EDGE,{"disambiguationData":[OSD([subQ0]),TDD([makeQuery(id+"F0.imprint","IMPRINT",EDGE,{"disambiguationData":[TD([[makeQuery(id+"F0.imprint","INTERSECT",VERTEX,{"disambiguationData":[OD(0.0)],"derivedFrom":[subQ0,sQuery(id+"F0.wireOp",EDGE,"E14.1.6")]}),1.0]])],"derivedFrom":subQ0})])],"isStart":true});}
            var Q18;
            Q18=makeQuery(id+"F1.opExtrude","CAP_EDGE",EDGE,{"disambiguationData":[OSD([sQuery(id+"F0.wireOp",EDGE,"E14.1.6")])],"isStart":true});
            var Q19;
            {var subQ0=sQuery(id+"F0.wireOp",EDGE,"E14.1.0");Q19=makeQuery(id+"F1.opExtrude","CAP_EDGE",EDGE,{"disambiguationData":[OSD([subQ0]),TDD([makeQuery(id+"F0.imprint","IMPRINT",EDGE,{"disambiguationData":[TD([[makeQuery(id+"F0.imprint","INTERSECT",VERTEX,{"disambiguationData":[OD(1.0)],"derivedFrom":[subQ0,sQuery(id+"F0.wireOp",EDGE,"E14.1.6")]}),-1.0]])],"derivedFrom":subQ0})])],"isStart":true});}
            var Q20;
            Q20=makeQuery(id+"F1.opExtrude","CAP_EDGE",EDGE,{"disambiguationData":[OSD([sQuery(id+"F0.wireOp",EDGE,"E14.1.5")])],"isStart":true});
            var Q21;
            {var subQ0=sQuery(id+"F0.wireOp",EDGE,"E14.1.0");Q21=makeQuery(id+"F1.opExtrude","CAP_EDGE",EDGE,{"disambiguationData":[OSD([subQ0]),TDD([makeQuery(id+"F0.imprint","IMPRINT",EDGE,{"disambiguationData":[TD([[makeQuery(id+"F0.imprint","INTERSECT",VERTEX,{"disambiguationData":[OD(1.0)],"derivedFrom":[subQ0,sQuery(id+"F0.wireOp",EDGE,"E14.1.5")]}),-1.0]])],"derivedFrom":subQ0})])],"isStart":true});}
            var Q22;
            Q22=makeQuery(id+"F1.opExtrude","CAP_EDGE",EDGE,{"disambiguationData":[OSD([sQuery(id+"F0.wireOp",EDGE,"E14.1.4")])],"isStart":true});
            var Q23;
            {var subQ0=sQuery(id+"F0.wireOp",EDGE,"E14.1.0");Q23=makeQuery(id+"F1.opExtrude","CAP_EDGE",EDGE,{"disambiguationData":[OSD([subQ0]),TDD([makeQuery(id+"F0.imprint","IMPRINT",EDGE,{"disambiguationData":[TD([[makeQuery(id+"F0.imprint","INTERSECT",VERTEX,{"disambiguationData":[OD(1.0)],"derivedFrom":[subQ0,sQuery(id+"F0.wireOp",EDGE,"E14.1.4")]}),-1.0]])],"derivedFrom":subQ0})])],"isStart":true});}
            var Q24;
            Q24=makeQuery(id+"F1.opExtrude","CAP_EDGE",EDGE,{"disambiguationData":[OSD([sQuery(id+"F0.wireOp",EDGE,"E14.1.3")])],"isStart":true});
            var Q25;
            {var subQ0=sQuery(id+"F0.wireOp",EDGE,"E14.1.0");Q25=makeQuery(id+"F1.opExtrude","CAP_EDGE",EDGE,{"disambiguationData":[OSD([subQ0]),TDD([makeQuery(id+"F0.imprint","IMPRINT",EDGE,{"disambiguationData":[TD([[makeQuery(id+"F0.imprint","INTERSECT",VERTEX,{"disambiguationData":[OD(1.0)],"derivedFrom":[subQ0,sQuery(id+"F0.wireOp",EDGE,"E14.1.3")]}),-1.0]])],"derivedFrom":subQ0})])],"isStart":true});}
            var Q26;
            Q26=makeQuery(id+"F1.opExtrude","CAP_EDGE",EDGE,{"disambiguationData":[OSD([sQuery(id+"F0.wireOp",EDGE,"E14.1.2")])],"isStart":true});
            var Q27;
            {var subQ0=sQuery(id+"F0.wireOp",EDGE,"E14.1.0");Q27=makeQuery(id+"F1.opExtrude","CAP_EDGE",EDGE,{"disambiguationData":[OSD([subQ0]),TDD([makeQuery(id+"F0.imprint","IMPRINT",EDGE,{"disambiguationData":[TD([[makeQuery(id+"F0.imprint","INTERSECT",VERTEX,{"disambiguationData":[OD(0.0)],"derivedFrom":[subQ0,sQuery(id+"F0.wireOp",EDGE,"E17.2.0")]}),1.0]])],"derivedFrom":subQ0})])],"isStart":true});}
            var Q28;
            Q28=makeQuery(id+"F1.opExtrude","CAP_EDGE",EDGE,{"disambiguationData":[OSD([sQuery(id+"F0.wireOp",EDGE,"E17.2.0")])],"isStart":true});
            var Q29;
            {var subQ0=sQuery(id+"F0.wireOp",EDGE,"E14.2.0");Q29=makeQuery(id+"F1.opExtrude","CAP_EDGE",EDGE,{"disambiguationData":[OSD([subQ0]),TDD([makeQuery(id+"F0.imprint","IMPRINT",EDGE,{"disambiguationData":[TD([[makeQuery(id+"F0.imprint","INTERSECT",VERTEX,{"disambiguationData":[OD(0.0)],"derivedFrom":[subQ0,sQuery(id+"F0.wireOp",EDGE,"E17.2.0")]}),-1.0]])],"derivedFrom":subQ0})])],"isStart":true});}
            var Q30;
            Q30=makeQuery(id+"F1.opExtrude","CAP_EDGE",EDGE,{"disambiguationData":[OSD([sQuery(id+"F0.wireOp",EDGE,"E14.2.7")])],"isStart":true});
            var Q31;
            {var subQ0=sQuery(id+"F0.wireOp",EDGE,"E14.2.0");Q31=makeQuery(id+"F1.opExtrude","CAP_EDGE",EDGE,{"disambiguationData":[OSD([subQ0]),TDD([makeQuery(id+"F0.imprint","IMPRINT",EDGE,{"disambiguationData":[TD([[makeQuery(id+"F0.imprint","INTERSECT",VERTEX,{"disambiguationData":[OD(0.0)],"derivedFrom":[subQ0,sQuery(id+"F0.wireOp",EDGE,"E14.2.6")]}),1.0]])],"derivedFrom":subQ0})])],"isStart":true});}
            var Q32;
            {var subQ0=sQuery(id+"F0.wireOp",EDGE,"E14.2.0");Q32=makeQuery(id+"F1.opExtrude","CAP_EDGE",EDGE,{"disambiguationData":[OSD([subQ0]),TDD([makeQuery(id+"F0.imprint","IMPRINT",EDGE,{"disambiguationData":[TD([[makeQuery(id+"F0.imprint","INTERSECT",VERTEX,{"disambiguationData":[OD(1.0)],"derivedFrom":[subQ0,sQuery(id+"F0.wireOp",EDGE,"E14.2.6")]}),-1.0]])],"derivedFrom":subQ0})])],"isStart":true});}
            var Q33;
            Q33=makeQuery(id+"F1.opExtrude","CAP_EDGE",EDGE,{"disambiguationData":[OSD([sQuery(id+"F0.wireOp",EDGE,"E14.2.6")])],"isStart":true});
            var Q34;
            Q34=makeQuery(id+"F1.opExtrude","CAP_EDGE",EDGE,{"disambiguationData":[OSD([sQuery(id+"F0.wireOp",EDGE,"E14.2.5")])],"isStart":true});
            var Q35;
            {var subQ0=sQuery(id+"F0.wireOp",EDGE,"E14.2.0");Q35=makeQuery(id+"F1.opExtrude","CAP_EDGE",EDGE,{"disambiguationData":[OSD([subQ0]),TDD([makeQuery(id+"F0.imprint","IMPRINT",EDGE,{"disambiguationData":[TD([[makeQuery(id+"F0.imprint","INTERSECT",VERTEX,{"disambiguationData":[OD(1.0)],"derivedFrom":[subQ0,sQuery(id+"F0.wireOp",EDGE,"E14.2.5")]}),-1.0]])],"derivedFrom":subQ0})])],"isStart":true});}
            var Q36;
            Q36=makeQuery(id+"F1.opExtrude","CAP_EDGE",EDGE,{"disambiguationData":[OSD([sQuery(id+"F0.wireOp",EDGE,"E14.2.4")])],"isStart":true});
            var Q37;
            {var subQ0=sQuery(id+"F0.wireOp",EDGE,"E14.2.0");Q37=makeQuery(id+"F1.opExtrude","CAP_EDGE",EDGE,{"disambiguationData":[OSD([subQ0]),TDD([makeQuery(id+"F0.imprint","IMPRINT",EDGE,{"disambiguationData":[TD([[makeQuery(id+"F0.imprint","INTERSECT",VERTEX,{"disambiguationData":[OD(1.0)],"derivedFrom":[subQ0,sQuery(id+"F0.wireOp",EDGE,"E14.2.4")]}),-1.0]])],"derivedFrom":subQ0})])],"isStart":true});}
            var Q38;
            Q38=makeQuery(id+"F1.opExtrude","CAP_EDGE",EDGE,{"disambiguationData":[OSD([sQuery(id+"F0.wireOp",EDGE,"E14.2.3")])],"isStart":true});
            var Q39;
            {var subQ0=sQuery(id+"F0.wireOp",EDGE,"E14.2.0");Q39=makeQuery(id+"F1.opExtrude","CAP_EDGE",EDGE,{"disambiguationData":[OSD([subQ0]),TDD([makeQuery(id+"F0.imprint","IMPRINT",EDGE,{"disambiguationData":[TD([[makeQuery(id+"F0.imprint","INTERSECT",VERTEX,{"disambiguationData":[OD(1.0)],"derivedFrom":[subQ0,sQuery(id+"F0.wireOp",EDGE,"E14.2.3")]}),-1.0]])],"derivedFrom":subQ0})])],"isStart":true});}
            var Q40;
            Q40=makeQuery(id+"F1.opExtrude","CAP_EDGE",EDGE,{"disambiguationData":[OSD([sQuery(id+"F0.wireOp",EDGE,"E14.2.2")])],"isStart":true});
            var Q41;
            {var subQ0=sQuery(id+"F0.wireOp",EDGE,"E14.2.0");Q41=makeQuery(id+"F1.opExtrude","CAP_EDGE",EDGE,{"disambiguationData":[OSD([subQ0]),TDD([makeQuery(id+"F0.imprint","IMPRINT",EDGE,{"disambiguationData":[TD([[makeQuery(id+"F0.imprint","INTERSECT",VERTEX,{"disambiguationData":[OD(0.0)],"derivedFrom":[subQ0,sQuery(id+"F0.wireOp",EDGE,"E16")]}),1.0]])],"derivedFrom":subQ0})])],"isStart":true});}
            fillet(context, id + "F3", {"entities" : qUnion([Q0, Q1, Q2, Q3, Q4, Q5, Q6, Q7, Q8, Q9, Q10, Q11, Q12, Q13, Q14, Q15, Q16, Q17, Q18, Q19, Q20, Q21, Q22, Q23, Q24, Q25, Q26, Q27, Q28, Q29, Q30, Q31, Q32, Q33, Q34, Q35, Q36, Q37, Q38, Q39, Q40, Q41]), "radius" : 2 * mm, "tangentPropagation" : true, "allowEdgeOverflow" : false});
        }
    });
